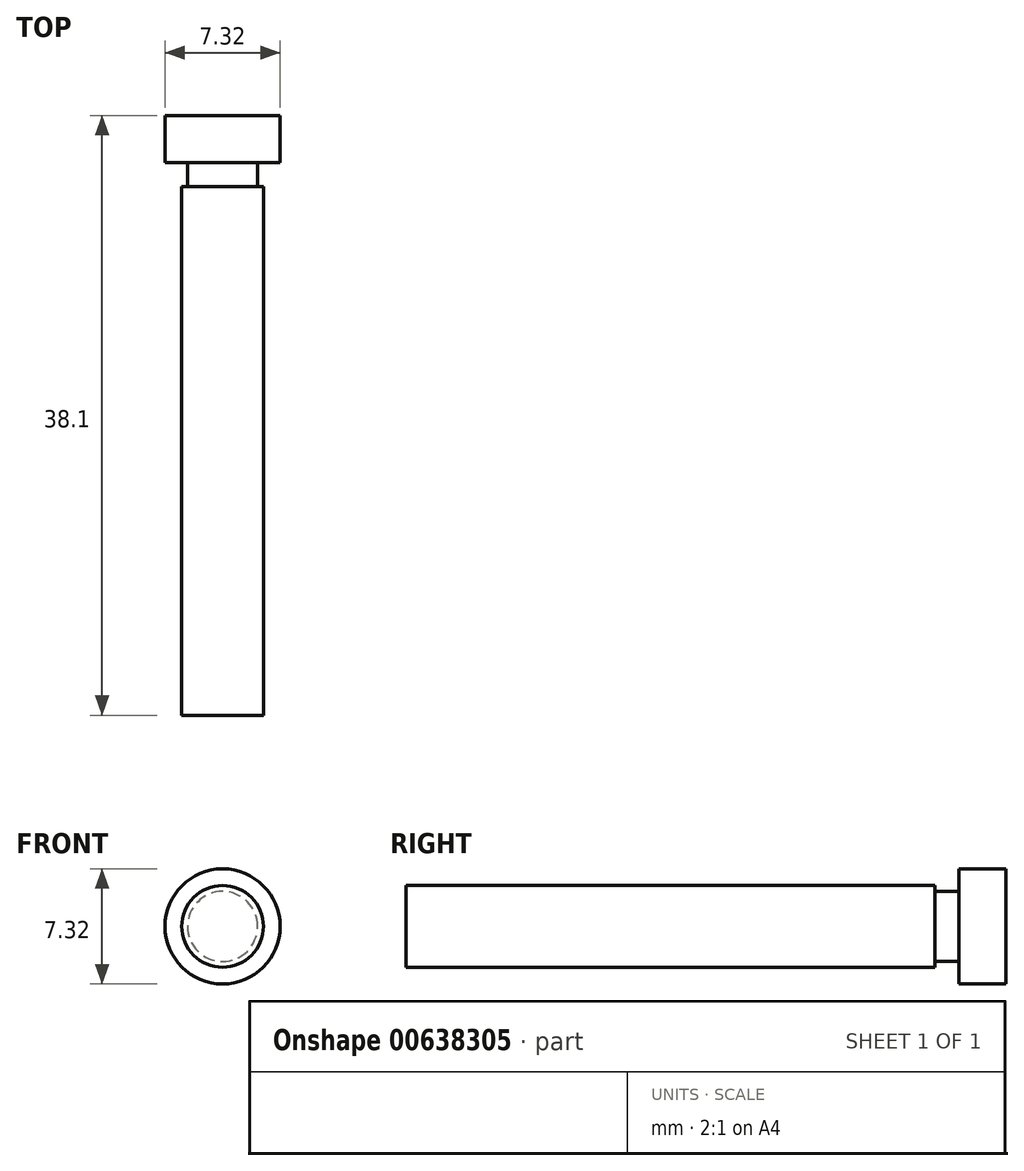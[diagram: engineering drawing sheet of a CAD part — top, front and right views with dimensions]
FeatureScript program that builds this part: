
annotation { "Feature Type Name" : "Feature", "Feature Type Description" : "" }
export const myFeature = defineFeature(function(context is Context, id is Id, definition is map)
    precondition{}
    {
        {
            var Q0;
            Q0=qCreatedBy(makeId("Top.planeOp"),FACE);
            var sketch = newSketch(context, id + "F0", { "sketchPlane" : qUnion([Q0])});
            skLineSegment(sketch, "E0", {"start": v(0, 0) * mm, "end": v(-3.66, 0) * mm});
            skLineSegment(sketch, "E1", {"start": v(-3.66, 0) * mm, "end": v(-3.66, -3) * mm});
            skLineSegment(sketch, "E2", {"start": v(-3.66, -3) * mm, "end": v(-2.22, -3) * mm});
            skLineSegment(sketch, "E3", {"start": v(-2.22, -3) * mm, "end": v(-2.22, -4.52) * mm});
            skLineSegment(sketch, "E4", {"start": v(-2.22, -4.52) * mm, "end": v(-2.6, -4.52) * mm});
            skLineSegment(sketch, "E5", {"start": v(-2.6, -4.52) * mm, "end": v(-2.6, -38.1) * mm});
            skLineSegment(sketch, "E6", {"start": v(-2.6, -38.1) * mm, "end": v(0, -38.1) * mm});
            skLineSegment(sketch, "E7", {"start": v(0, -38.1) * mm, "end": v(0, 0) * mm});
            skSolve(sketch);
        }
        {
            var Q0;
            Q0=makeQuery(id+"F0.imprint","IMPRINT",FACE,{"disambiguationData":[TD([[makeQuery(id+"F0.imprint","IMPRINT",EDGE,{"derivedFrom":sQuery(id+"F0.wireOp",EDGE,"E0")}),1.0]])]});
            var Q1;
            Q1=sQuery(id+"F0.wireOp",EDGE,"E7");
            revolve(context, id + "F1", {"entities" : qUnion([Q0]), "axis" : qUnion([Q1]), "revolveType" : RevolveType.FULL});
        }
    });
